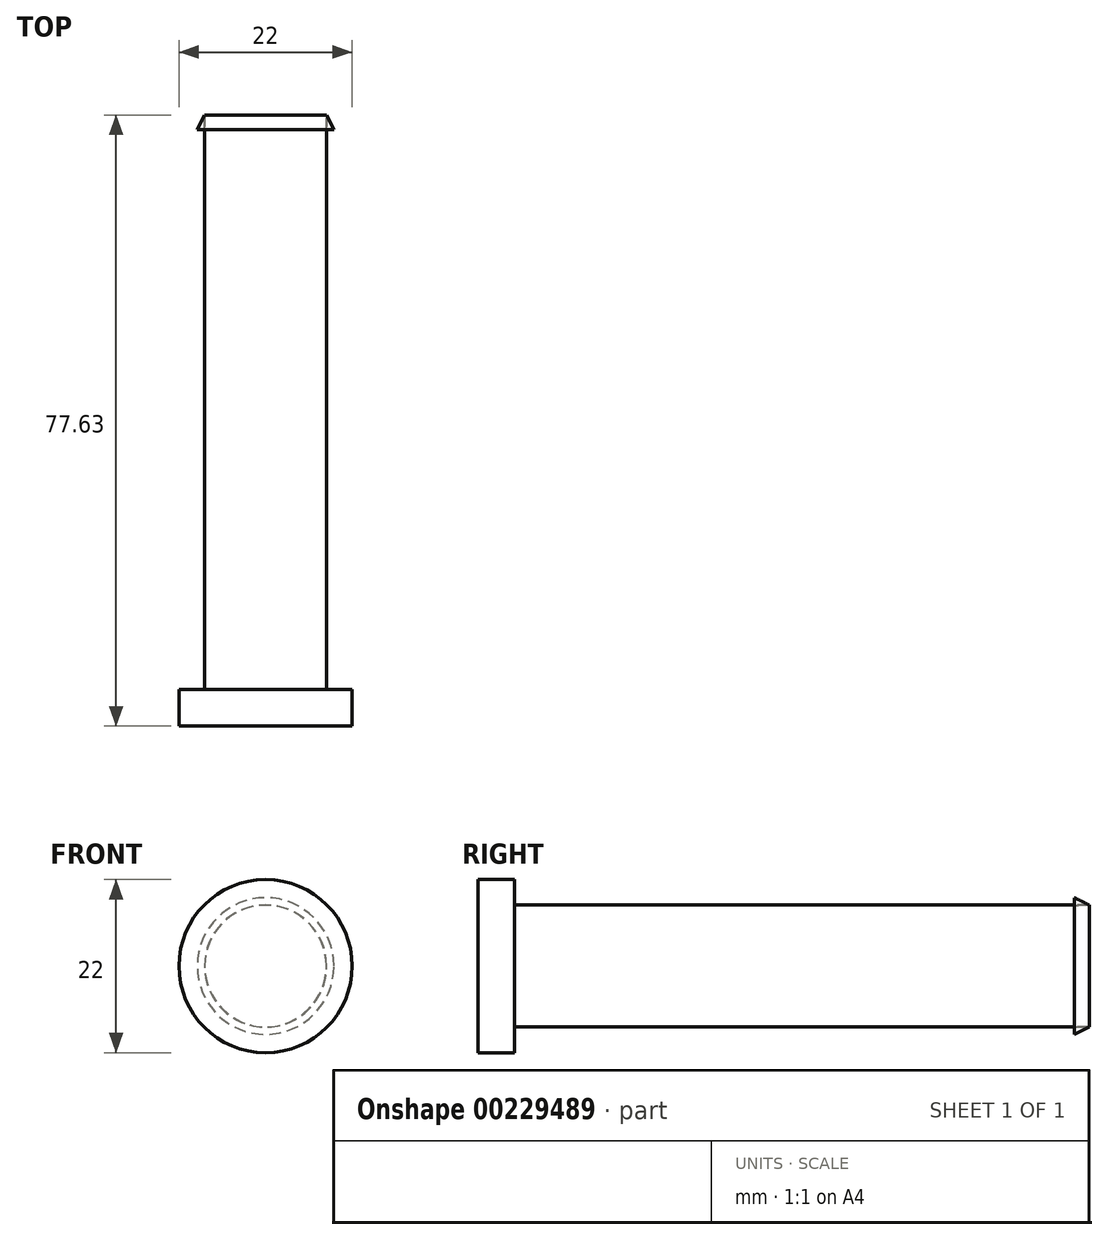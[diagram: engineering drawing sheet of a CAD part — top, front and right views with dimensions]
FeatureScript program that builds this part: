
annotation { "Feature Type Name" : "Feature", "Feature Type Description" : "" }
export const myFeature = defineFeature(function(context is Context, id is Id, definition is map)
    precondition{}
    {
        {
            var Q0;
            Q0=qCreatedBy(makeId("Front.planeOp"),FACE);
            var sketch = newSketch(context, id + "F0", { "sketchPlane" : qUnion([Q0])});
            skCircle(sketch, "E0", {"center": v(0, 0) * mm, "radius": 9.5 * mm});
            skCircle(sketch, "E1", {"center": v(0, 0) * mm, "radius": 7.75 * mm});
            skSolve(sketch);
        }
        {
            var Q0;
            Q0=makeQuery(id+"F0.imprint","IMPRINT",FACE,{"disambiguationData":[TD([[makeQuery(id+"F0.imprint","IMPRINT",EDGE,{"derivedFrom":sQuery(id+"F0.wireOp",EDGE,"E1")}),1.0]])]});
            extrude(context, id + "F1", {"entities" : qUnion([Q0]), "oppositeDirection" : true, "depth" : 73 * mm});
        }
        {
            var Q0;
            Q0=qCreatedBy(makeId("Right.planeOp"),FACE);
            var sketch = newSketch(context, id + "F2", { "sketchPlane" : qUnion([Q0])});
            skLineSegment(sketch, "E2", {"start": v(72.99, 7.75) * mm, "end": v(71.12, 8.68) * mm});
            skLineSegment(sketch, "E3", {"start": v(71.12, 8.68) * mm, "end": v(71.12, 7.73) * mm});
            skLineSegment(sketch, "E4", {"start": v(71.12, 7.73) * mm, "end": v(72.99, 7.75) * mm});
            skSolve(sketch);
        }
        {
            var Q0;
            Q0=makeQuery(id+"F2.imprint","IMPRINT",FACE,{"disambiguationData":[TD([[makeQuery(id+"F2.imprint","IMPRINT",EDGE,{"derivedFrom":sQuery(id+"F2.wireOp",EDGE,"E2")}),1.0]])]});
            var Q1;
            Q1=makeQuery(id+"F1.opExtrude","CAP_EDGE",EDGE,{"disambiguationData":[OSD([sQuery(id+"F0.wireOp",EDGE,"E1")])],"isStart":false});
            revolve(context, id + "F3", {"entities" : qUnion([Q0]), "axis" : qUnion([Q1]), "revolveType" : RevolveType.FULL});
        }
        {
            var Q0;
            Q0=qCreatedBy(makeId("Front.planeOp"),FACE);
            var sketch = newSketch(context, id + "F4", { "sketchPlane" : qUnion([Q0])});
            skCircle(sketch, "E5.0", {"center": v(0, 0) * mm, "radius": 8.68 * mm});
            skLineSegment(sketch, "E6.0", {"start": v(-9, -1) * mm, "end": v(9, -1) * mm});
            skLineSegment(sketch, "E7.0", {"start": v(-9, 1) * mm, "end": v(9, 1) * mm});
            skLineSegment(sketch, "E8.0", {"start": v(-9, 1) * mm, "end": v(-9, -1) * mm});
            skLineSegment(sketch, "E9.0", {"start": v(9, 1) * mm, "end": v(9, -1) * mm});
            skSolve(sketch);
        }
        {
            var Q0;
            {var subQ0=sQuery(id+"F4.wireOp",EDGE,"E7.0");var subQ1=sQuery(id+"F4.wireOp",EDGE,"E5.0");var subQ2=makeQuery(id+"F4.imprint","INTERSECT",VERTEX,{"disambiguationData":[OD(0.0)],"derivedFrom":[subQ1,subQ0]});Q0=makeQuery(id+"F4.imprint","IMPRINT",FACE,{"disambiguationData":[TD([[makeQuery(id+"F4.imprint","IMPRINT",EDGE,{"disambiguationData":[TD([[subQ2,1.0]])],"derivedFrom":subQ1}),-1.0]])]});}
            var Q1;
            {var subQ5=sQuery(id+"F4.wireOp",EDGE,"E8.0");Q1=makeQuery(id+"F4.imprint","IMPRINT",FACE,{"disambiguationData":[TD([[makeQuery(id+"F4.imprint","IMPRINT",EDGE,{"derivedFrom":subQ5}),1.0]])]});}
            var Q2;
            {var subQ5=sQuery(id+"F4.wireOp",EDGE,"E9.0");Q2=makeQuery(id+"F4.imprint","IMPRINT",FACE,{"disambiguationData":[TD([[makeQuery(id+"F4.imprint","IMPRINT",EDGE,{"derivedFrom":subQ5}),-1.0]])]});}
            extrude(context, id + "F5", {"entities" : qUnion([Q0, Q1, Q2]), "operationType" : NewBodyOperationType.REMOVE, "oppositeDirection" : true, "depth" : 80 * mm, "hasSecondDirection" : true, "secondDirectionOppositeDirection" : true, "secondDirectionDepth" : 47 * mm});
        }
        {
            var Q0;
            Q0=qCreatedBy(makeId("Right.planeOp"),FACE);
            var sketch = newSketch(context, id + "F6", { "sketchPlane" : qUnion([Q0])});
            skLineSegment(sketch, "E10", {"start": v(0, 0) * mm, "end": v(0, 11) * mm});
            skLineSegment(sketch, "E11", {"start": v(0, 11) * mm, "end": v(-4.63, 11) * mm});
            skPoint(sketch, "E12.endSnap0", {"position": v(-4.63, 0) * mm});
            skLineSegment(sketch, "E13", {"start": v(-4.63, 11) * mm, "end": v(-4.63, 0) * mm});
            skLineSegment(sketch, "E14", {"start": v(0, 0) * mm, "end": v(-4.63, 0) * mm});
            skLineSegment(sketch, "E15", {"start": v(11.55, 0) * mm, "end": v(-20.08, 0) * mm, "construction": true});
            skSolve(sketch);
        }
        {
            var Q0;
            Q0=makeQuery(id+"F6.imprint","IMPRINT",FACE,{"disambiguationData":[TD([[makeQuery(id+"F6.imprint","IMPRINT",EDGE,{"derivedFrom":sQuery(id+"F6.wireOp",EDGE,"E10")}),1.0]])]});
            var Q1;
            Q1=sQuery(id+"F6.wireOp",EDGE,"E15");
            revolve(context, id + "F7", {"operationType" : NewBodyOperationType.ADD, "entities" : qUnion([Q0]), "axis" : qUnion([Q1]), "revolveType" : RevolveType.FULL});
        }
    });
